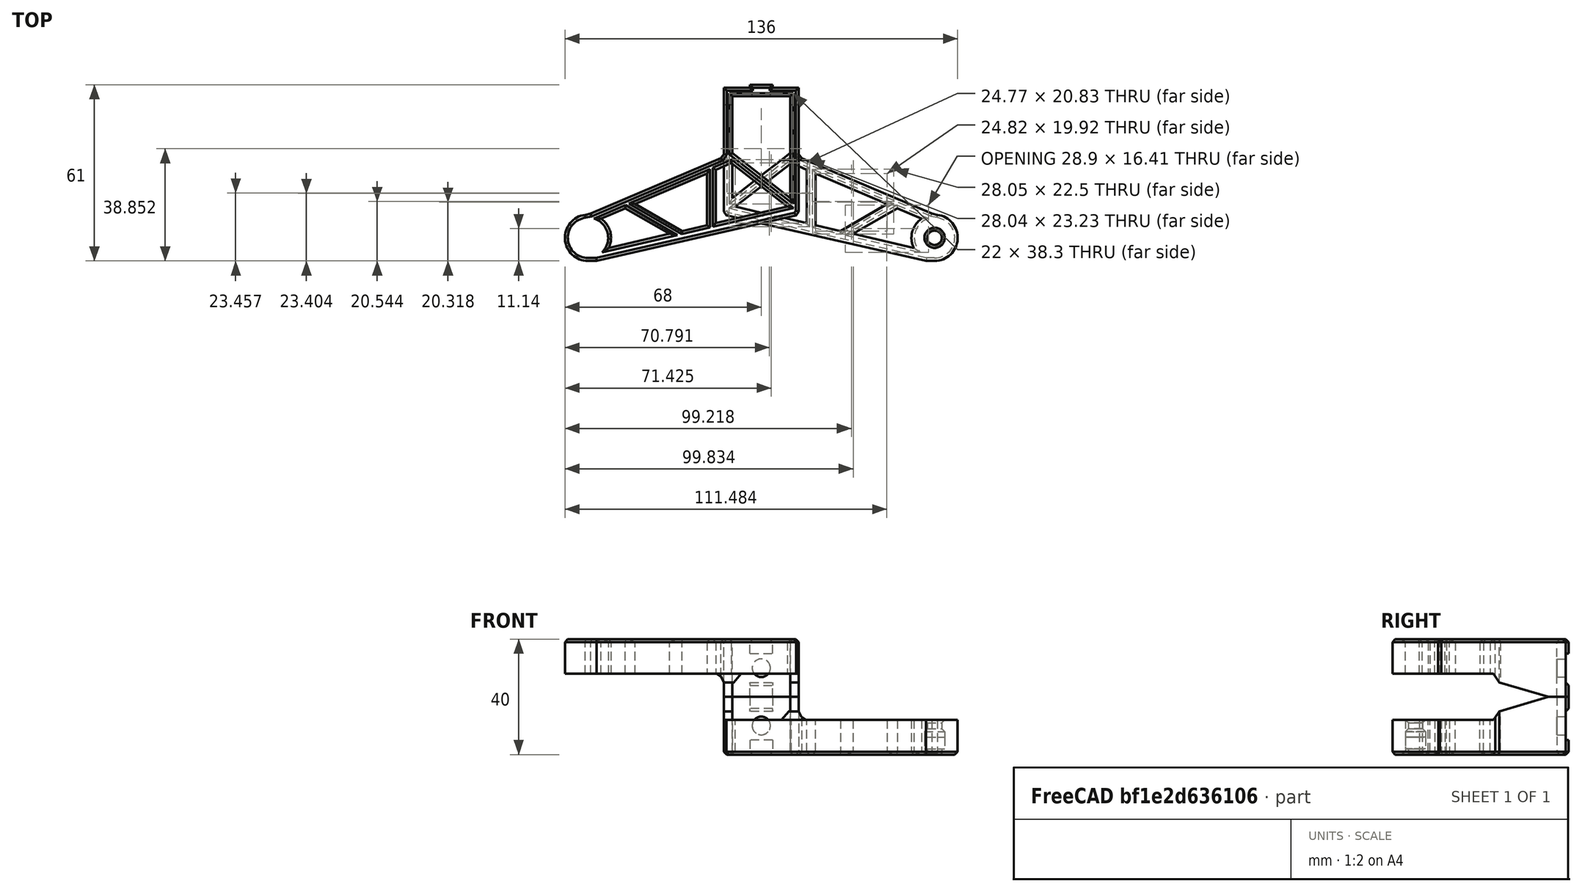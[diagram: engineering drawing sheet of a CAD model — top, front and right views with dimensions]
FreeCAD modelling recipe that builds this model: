
FCSTD DOCUMENT  (FreeCAD 0.19R24291 (Git))
Label: filament-guide
License: Other
LicenseURL: GPL3
objects: Part::Feature×4, Part::Chamfer×3, Part::Cylinder×2, Part::Cut×2, Part::MultiFuse×1, Part::Box×1
note: 13 computed .brp shape members not serialized (recipe doc carries the construction recipe); baked Part::Feature solids carry a one-line shape summary decoded from their .brp

FEATURE [Part::Feature] Cut004001001
  shape: bbox 81 x 61 x 20 mm, 69 faces (baked)
FEATURE [Part::Feature] Cut004006001001  label="collet-slot"
  Placement = pos=(-60,-50,13) rot=(0,0,1;0rad)
  shape: bbox 7 x 7 x 7 mm, 9 faces (baked)
FEATURE [Part::Cylinder] Cylinder
  Angle = 360
  AttacherType = Attacher::AttachEngine3D
  Height = 15
  Placement = pos=(-60,-50,0) rot=(0,0,1;0rad)
  Radius = 2.5
FEATURE [Part::Cylinder] Cylinder001
  Angle = 360
  AttacherType = Attacher::AttachEngine3D
  Height = 3
  Placement = pos=(-60,-50,11) rot=(0,0,1;0rad)
  Radius = 3.5
FEATURE [Part::Chamfer] Chamfer
  Base = -> Cylinder001
  Edges = 1 edges r=1: [Edge3]
FEATURE [Part::MultiFuse] Fusion
  Shapes = -> [Chamfer,Cylinder,Cut004006001001]
FEATURE [Part::Box] Box  label="Cube"
  AttacherType = Attacher::AttachEngine3D
  Height = 10
  Length = 10
  Placement = pos=(-5,2,5) rot=(0,0,1;0rad)
  Width = 10
FEATURE [Part::Cut] Cut
  Base = -> Cut004001001
  Tool = -> Box
FEATURE [Part::Chamfer] Chamfer001  label="arm-base"
  Base = -> Cut
  Edges = 1 edges r=0.99: [Edge75]
FEATURE [Part::Feature] Chamfer001001  label="arm-base001"
  shape: bbox 81 x 61 x 20 mm, 78 faces (baked)
FEATURE [Part::Cut] Cut004006001002
  Base = -> Chamfer001001
  Tool = -> Fusion
FEATURE [Part::Chamfer] Chamfer001002  label="filament-guide-e3d-collet"
  Base = -> Cut004006001002
  Edges = 1 edges r=1: [Edge131]
  Placement = pos=(0,0,0) rot=(0,1,0;3.14159rad)
FEATURE [Part::Feature] Chamfer001002001001  label="filament-guide-e3d-collet002"
  shape: bbox 81 x 61 x 20 mm, 85 faces (baked)
